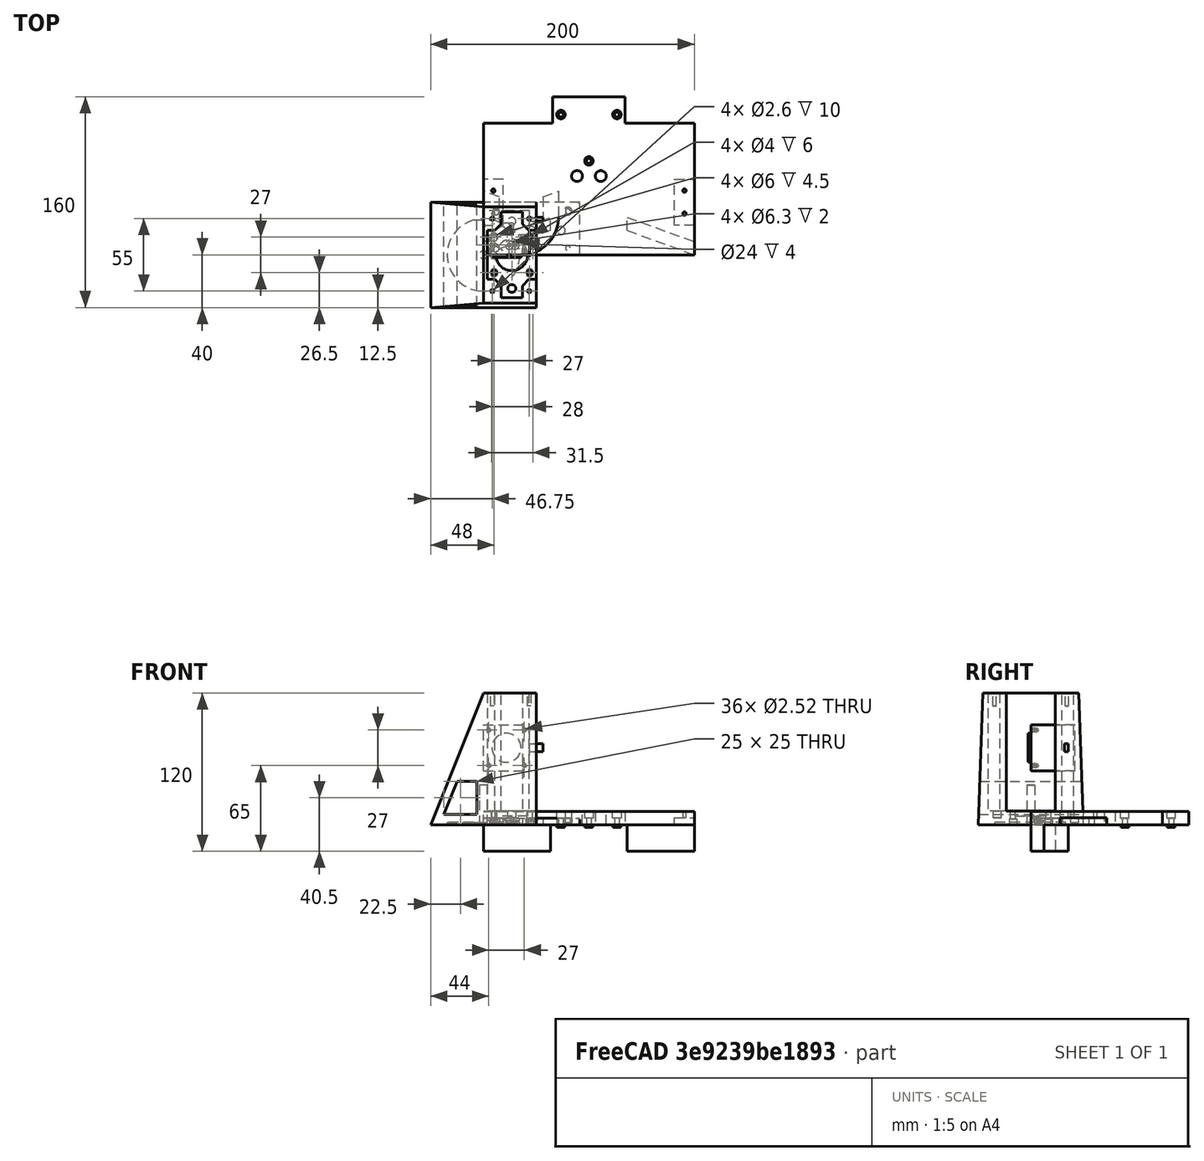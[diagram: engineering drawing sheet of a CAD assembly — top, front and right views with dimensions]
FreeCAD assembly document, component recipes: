
FREECAD ASSEMBLY — COMPONENT RECIPES ("charging-station")

This assembly document has 9 components, labeled P0..P8 below (a component is one placed body or linked part). 9 of them carry a construction recipe — the FreeCAD feature program that regenerates the part from scratch, quoted from this document or its linked companion documents; the rest are supplied as boundary geometry only. No exploded tour is included for this assembly.
COMPONENT P0 — recipe-attached ("Beam", modeled in this document).
Construction recipe (the document's own serialized feature program — sketch geometry with constraints, then the solid features built on it; lengths are millimeters unless a unit is written):

FEATURE [Sketcher::SketchObject] Sketch
  ArcFitTolerance = 0
  AttachmentSupport = -> [XY_Plane]
  FullyConstrained = true
  MakeInternals = false
  MapMode = 5
  sketch-geometry (4):
    g0: LineSegment StartX=0 StartY=0 StartZ=0 EndX=160 EndY=0 EndZ=0
    g1: LineSegment StartX=160 StartY=0 StartZ=0 EndX=160 EndY=100 EndZ=0
    g2: LineSegment StartX=160 StartY=100 StartZ=0 EndX=0 EndY=100 EndZ=0
    g3: LineSegment StartX=0 StartY=100 StartZ=0 EndX=0 EndY=0 EndZ=0
  constraints (11):
    c: Coincident(g0,g1)
    c: Coincident(g1,g2)
    c: Coincident(g2,g3)
    c: Coincident(g3,g0)
    c: Horizontal(g0)
    c: Horizontal(g2)
    c: Vertical(g1)
    c: Vertical(g3)
    c: Coincident(g0,g-1)
    c: DistanceY(g1,g1) = 100
    c: DistanceX(g0,g0) = 160
FEATURE [PartDesign::Pad] Pad
  Direction = (0,0,1)
  Length = 10
  Length2 = 10
  Profile = -> Sketch
  ReferenceAxis = -> Sketch [N_Axis]
  Suppressed = false
  Type = 0
FEATURE [Sketcher::SketchObject] Sketch001
  ArcFitTolerance = 0
  AttachmentSupport = -> [Pad]
  ExternalGeometry = -> [Pad]
  FullyConstrained = true
  MakeInternals = false
  MapMode = 5
  Placement = pos=(0,0,0) rot=(1,0,0;3.14159rad)
  sketch-geometry (15):
    g0: LineSegment [constr] StartX=63.5 StartY=-33.1121 StartZ=0 EndX=96.5 EndY=-33.1121 EndZ=0
    g1: LineSegment StartX=0 StartY=-10 StartZ=0 EndX=0 EndY=0 EndZ=0
    g2: LineSegment [constr] StartX=63.5 StartY=-23.1121 StartZ=0 EndX=63.5 EndY=-33.1121 EndZ=0
    g3: LineSegment [constr] StartX=96.5 StartY=-33.1121 StartZ=0 EndX=96.5 EndY=-23.1121 EndZ=0
    g4: LineSegment StartX=160 StartY=0 StartZ=0 EndX=160 EndY=-10 EndZ=0
    g5: LineSegment StartX=51 StartY=-18.5625 StartZ=0 EndX=51 EndY=-28.5625 EndZ=0
    g6: LineSegment StartX=0 StartY=-10 StartZ=0 EndX=51 EndY=-28.5625 EndZ=0
    g7: LineSegment [constr] StartX=51 StartY=-28.5625 StartZ=0 EndX=63.5 EndY=-33.1121 EndZ=0
    g8: LineSegment [constr] StartX=63.5 StartY=-23.1121 StartZ=0 EndX=51 EndY=-18.5625 EndZ=0
    g9: LineSegment StartX=51 StartY=-18.5625 StartZ=0 EndX=0 EndY=0 EndZ=0
    g10: LineSegment StartX=109 StartY=-18.5625 StartZ=0 EndX=109 EndY=-28.5625 EndZ=0
    g11: LineSegment [constr] StartX=96.5 StartY=-23.1121 StartZ=0 EndX=109 EndY=-18.5625 EndZ=0
    g12: LineSegment StartX=109 StartY=-18.5625 StartZ=0 EndX=160 EndY=0 EndZ=0
    g13: LineSegment [constr] StartX=96.5 StartY=-33.1121 StartZ=0 EndX=109 EndY=-28.5625 EndZ=0
    g14: LineSegment StartX=109 StartY=-28.5625 StartZ=0 EndX=160 EndY=-10 EndZ=0
  constraints (40):
    c: DistanceX(g0,g0) = 33
    c: Horizontal(g0)
    c: Vertical(g3)
    c: Vertical(g4)
    c: Vertical(g2)
    c: Equal(g2,g3)
    c: DistanceY(g4,g4) = 10
    c: Coincident(g1,g-1)
    c: Vertical(g1)
    c: Vertical(g5)
    c: DistanceX(g5,g0) = 12.5
    c: Coincident(g1,g6)
    c: Coincident(g6,g5)
    c: Coincident(g6,g7)
    c: Coincident(g7,g2)
    c: Coincident(g2,g8)
    c: Coincident(g8,g5)
    c: Coincident(g8,g9)
    c: Coincident(g9,g1)
    c: Vertical(g10)
    c: Coincident(g3,g11)
    c: Coincident(g11,g10)
    c: Coincident(g11,g12)
    c: Coincident(g3,g13)
    c: Coincident(g13,g10)
    c: Coincident(g13,g14)
    c: Coincident(g14,g4)
    c: Equal(g13,g7)
    c: Coincident(g2,g0)
    c: Coincident(g3,g0)
    c: Parallel(g6,g9)
    c: Parallel(g14,g12)
    c: Parallel(g7,g8)
    c: Parallel(g13,g11)
    c: Parallel(g13,g14)
    c: Parallel(g7,g6)
    c: Angle(g-1,g12) = 0.349066
    c: Equal(g14,g6)
    c: Coincident(g12,g-3)
    c: Coincident(g4,g12)
FEATURE [PartDesign::Pad] Pad008
  BaseFeature = -> Pad
  Direction = (0,0,-1)
  Length = 20
  Length2 = 10
  Profile = -> Sketch001
  ReferenceAxis = -> Sketch001 [N_Axis]
  Refine = true
  Suppressed = false
  Type = 0
FEATURE [Sketcher::SketchObject] Sketch029
  ArcFitTolerance = 0
  AttachmentSupport = -> [Pad008]
  ExternalGeometry = -> [Pad008]
  FullyConstrained = true
  MakeInternals = false
  MapMode = 5
  Placement = pos=(0,0,0) rot=(1,0,0;3.14159rad)
  sketch-geometry (16):
    g0: GeomPoint [constr] X=80 Y=-52.2941 Z=0
    g1: LineSegment [constr] StartX=80 StartY=-52.2941 StartZ=0 EndX=80 EndY=-59.7941 EndZ=0
    g2: LineSegment [constr] StartX=71 StartY=-59.7941 StartZ=0 EndX=89 EndY=-59.7941 EndZ=0
    g3: Circle CenterX=71 CenterY=-59.7941 CenterZ=0 NormalX=0 NormalY=0 NormalZ=1 AngleXU=0 Radius=4.15
    g4: Circle CenterX=89 CenterY=-59.7941 CenterZ=0 NormalX=0 NormalY=0 NormalZ=1 AngleXU=0 Radius=4.15
    g5: LineSegment [constr] StartX=51 StartY=-18.5625 StartZ=0 EndX=80 EndY=-29.1176 EndZ=0
    g6: LineSegment [constr] StartX=80 StartY=-29.1176 StartZ=0 EndX=109 EndY=-18.5625 EndZ=0
    g7: LineSegment [constr] StartX=51 StartY=-28.5625 StartZ=0 EndX=80 EndY=-39.1176 EndZ=0
    g8: LineSegment [constr] StartX=80 StartY=-39.1176 StartZ=0 EndX=109 EndY=-28.5625 EndZ=0
    g9: LineSegment [constr] StartX=64 StartY=-23.2941 StartZ=0 EndX=64 EndY=-43.2941 EndZ=0
    g10: LineSegment [constr] StartX=64 StartY=-43.2941 StartZ=0 EndX=74 EndY=-43.2941 EndZ=0
    g11: LineSegment [constr] StartX=74 StartY=-43.2941 StartZ=0 EndX=74 EndY=-52.2941 EndZ=0
    g12: LineSegment [constr] StartX=74 StartY=-52.2941 StartZ=0 EndX=86 EndY=-52.2941 EndZ=0
    g13: LineSegment [constr] StartX=86 StartY=-52.2941 StartZ=0 EndX=86 EndY=-43.2941 EndZ=0
    g14: LineSegment [constr] StartX=86 StartY=-43.2941 StartZ=0 EndX=96 EndY=-43.2941 EndZ=0
    g15: LineSegment [constr] StartX=96 StartY=-43.2941 StartZ=0 EndX=96 EndY=-23.2941 EndZ=0
  constraints (43):
    c: Coincident(g1,g0)
    c: Vertical(g1)
    c: Horizontal(g2)
    c: Symmetric(g2,g2,g1)
    c: Coincident(g3,g2)
    c: Coincident(g4,g2)
    c: Diameter(g4) = 8.3
    c: Equal(g4,g3)
    c: DistanceX(g2,g2) = 18
    c: Coincident(g5,g6)
    c: Angle(g5,g-1) = 0.349066
    c: Equal(g6,g5)
    c: Coincident(g7,g8)
    c: Parallel(g8,g6)
    c: Parallel(g7,g5)
    c: Coincident(g7,g-4)
    c: Vertical(g9)
    c: Coincident(g9,g10)
    c: Horizontal(g10)
    c: Coincident(g10,g11)
    c: Vertical(g11)
    c: Coincident(g11,g12)
    c: Horizontal(g12)
    c: Coincident(g12,g13)
    c: Coincident(g13,g14)
    c: Coincident(g14,g15)
    c: Vertical(g15)
    c: Horizontal(g14)
    c: Vertical(g13)
    c: Symmetric(g11,g12,g0)
    c: DistanceY(g15,g15) = 20
    c: Equal(g11,g13)
    c: Equal(g9,g15)
    c: Coincident(g5,g-3)
    c: DistanceY(g12,g14) = 9
    c: Equal(g10,g14)
    c: DistanceX(g12,g12) = 12
    c: DistanceY(g2,g12) = 7.5
    c: PointOnObject(g9,g5)
    c: PointOnObject(g15,g6)
    c: DistanceX(g9,g15) = 32
    c: Coincident(g8,g-5)
    c: Coincident(g6,g-5)
FEATURE [PartDesign::Pocket] Pocket017
  BaseFeature = -> Pad008
  Direction = (0,0,1)
  Length = 5
  Length2 = 5
  Profile = -> Sketch029
  ReferenceAxis = -> Sketch029 [N_Axis]
  Refine = true
  Suppressed = false
  Type = 2
FEATURE [Sketcher::SketchObject] Sketch031
  ArcFitTolerance = 0
  AttachmentSupport = -> [Pocket017]
  ExternalGeometry = -> [Pocket017]
  FullyConstrained = true
  MakeInternals = false
  MapMode = 5
  Placement = pos=(0,100,0) rot=(0,0.707107,0.707107;3.14159rad)
  sketch-geometry (6):
    g0: LineSegment StartX=-107.5 StartY=0 StartZ=0 EndX=-52.5 EndY=0 EndZ=0
    g1: LineSegment StartX=-52.5 StartY=0 StartZ=0 EndX=-52.5 EndY=10 EndZ=0
    g2: LineSegment StartX=-52.5 StartY=10 StartZ=0 EndX=-107.5 EndY=10 EndZ=0
    g3: LineSegment StartX=-107.5 StartY=10 StartZ=0 EndX=-107.5 EndY=0 EndZ=0
    g4: GeomPoint X=-80 Y=10 Z=0
    g5: GeomPoint X=-80 Y=10 Z=0
  constraints (13):
    c: Coincident(g0,g1)
    c: Coincident(g1,g2)
    c: Coincident(g2,g3)
    c: Coincident(g3,g0)
    c: Horizontal(g0)
    c: Horizontal(g2)
    c: Vertical(g1)
    c: Vertical(g3)
    c: PointOnObject(g0,g-1)
    c: Symmetric(g2,g2,g4)
    c: Symmetric(g-3,g-3,g5)
    c: Coincident(g4,g5)
    c: DistanceX(g2,g2) = 55
FEATURE [PartDesign::Pad] Pad010
  BaseFeature = -> Pocket017
  Direction = (0,1,-2e-16)
  Length = 20
  Length2 = 10
  Profile = -> Sketch031
  ReferenceAxis = -> Sketch031 [N_Axis]
  Refine = true
  Suppressed = false
  Type = 0
FEATURE [Sketcher::SketchObject] Sketch032
  ArcFitTolerance = 0
  AttachmentSupport = -> [Pad010]
  ExternalGeometry = -> [Pad010]
  FullyConstrained = true
  MakeInternals = false
  MapMode = 5
  Placement = pos=(0,0,-4e-16) rot=(1,0,0;3.14159rad)
  sketch-geometry (11):
    g0: Circle [constr] CenterX=80 CenterY=-95.2941 CenterZ=0 NormalX=0 NormalY=0 NormalZ=1 AngleXU=0 Radius=27.5
    g1: GeomPoint [constr] X=80 Y=-59.7941 Z=0
    g2: LineSegment [constr] StartX=80 StartY=-59.7941 StartZ=0 EndX=80 EndY=-95.2941 EndZ=0
    g3: LineSegment [constr] StartX=71 StartY=-67.7941 StartZ=0 EndX=89 EndY=-67.7941 EndZ=0
    g4: Circle CenterX=80 CenterY=-71.2941 CenterZ=0 NormalX=0 NormalY=0 NormalZ=1 AngleXU=0 Radius=3
    g5: Circle CenterX=101.25 CenterY=-106.449 CenterZ=0 NormalX=0 NormalY=0 NormalZ=1 AngleXU=0 Radius=3
    g6: Circle CenterX=58.75 CenterY=-106.449 CenterZ=0 NormalX=0 NormalY=0 NormalZ=1 AngleXU=0 Radius=3
    g7: LineSegment [constr] StartX=58.75 StartY=-106.449 StartZ=0 EndX=101.25 EndY=-106.449 EndZ=0
    g8: LineSegment [constr] StartX=80 StartY=-106.449 StartZ=0 EndX=80 EndY=-95.2941 EndZ=0
    g9: Circle [constr] CenterX=101.25 CenterY=-106.449 CenterZ=0 NormalX=0 NormalY=0 NormalZ=1 AngleXU=0 Radius=1.5
    g10: Circle [constr] CenterX=80 CenterY=-71.2941 CenterZ=0 NormalX=0 NormalY=0 NormalZ=1 AngleXU=0 Radius=1.5
  constraints (27):
    c: Diameter(g0) = 55
    c: Symmetric(g-4,g-3,g1)
    c: Coincident(g2,g1)
    c: Vertical(g2)
    c: Coincident(g0,g2)
    c: Horizontal(g3)
    c: Tangent(g3,g0)
    c: Distance(g-4,g3) = 8
    c: PointOnObject(g4,g2)
    c: Diameter(g4) = 6
    c: Equal(g6,g5)
    c: Equal(g5,g4)
    c: Horizontal(g6,g5)
    c: DistanceX(g6,g5) = 42.5
    c: Coincident(g7,g6)
    c: Coincident(g7,g5)
    c: Symmetric(g7,g7,g8)
    c: Coincident(g8,g0)
    c: Vertical(g8)
    c: Vertical(g3,g-3)
    c: Vertical(g3,g-4)
    c: Coincident(g9,g5)
    c: Diameter(g9) = 3
    c: Distance(g0,g9) = 2
    c: Coincident(g10,g4)
    c: Diameter(g10) = 3
    c: Distance(g10,g0) = 2
FEATURE [PartDesign::Pad] Pad011
  BaseFeature = -> Pad010
  Direction = (0,0,-1)
  Length = 2
  Length2 = 10
  Profile = -> Sketch032
  ReferenceAxis = -> Sketch032 [N_Axis]
  Refine = true
  Suppressed = false
  Type = 0
FEATURE [Sketcher::SketchObject] Sketch033
  ArcFitTolerance = 0
  AttachmentSupport = -> [Pad011]
  ExternalGeometry = -> [Pad011]
  FullyConstrained = true
  MakeInternals = false
  MapMode = 5
  Placement = pos=(0,0,-2) rot=(1,0,0;3.14159rad)
  sketch-geometry (3):
    g0: Circle CenterX=58.75 CenterY=-106.449 CenterZ=0 NormalX=0 NormalY=0 NormalZ=1 AngleXU=0 Radius=1.85
    g1: Circle CenterX=101.25 CenterY=-106.449 CenterZ=0 NormalX=0 NormalY=0 NormalZ=1 AngleXU=0 Radius=1.85
    g2: Circle CenterX=80 CenterY=-71.2941 CenterZ=0 NormalX=0 NormalY=0 NormalZ=1 AngleXU=0 Radius=1.85
  constraints (6):
    c: Coincident(g0,g-4)
    c: Coincident(g1,g-5)
    c: Coincident(g2,g-3)
    c: Equal(g2,g0)
    c: Equal(g0,g1)
    c: Diameter(g2) = 3.7
FEATURE [PartDesign::Pocket] Pocket018
  BaseFeature = -> Pad011
  Direction = (0,0,1)
  Length = 5
  Length2 = 5
  Profile = -> Sketch033
  ReferenceAxis = -> Sketch033 [N_Axis]
  Refine = true
  Suppressed = false
  Type = 1
FEATURE [Sketcher::SketchObject] Sketch034
  ArcFitTolerance = 0
  AttachmentSupport = -> [Pocket018]
  ExternalGeometry = -> [Pocket018]
  FullyConstrained = true
  MakeInternals = false
  MapMode = 5
  Placement = pos=(0,0,10) rot=(0,0,1;0rad)
  sketch-geometry (3):
    g0: Circle CenterX=58.75 CenterY=106.449 CenterZ=0 NormalX=0 NormalY=0 NormalZ=1 AngleXU=0 Radius=3.25
    g1: Circle CenterX=101.25 CenterY=106.449 CenterZ=0 NormalX=0 NormalY=0 NormalZ=1 AngleXU=0 Radius=3.25
    g2: Circle CenterX=80 CenterY=71.2941 CenterZ=0 NormalX=0 NormalY=0 NormalZ=1 AngleXU=0 Radius=3.25
  constraints (6):
    c: Coincident(g0,g-3)
    c: Equal(g2,g0)
    c: Equal(g0,g1)
    c: Diameter(g0) = 6.5
    c: Coincident(g1,g-5)
    c: Coincident(g2,g-4)
FEATURE [PartDesign::Pocket] Pocket019
  BaseFeature = -> Pocket018
  Direction = (0,0,-1)
  Length = 5
  Length2 = 5
  Profile = -> Sketch034
  ReferenceAxis = -> Sketch034 [N_Axis]
  Refine = true
  Suppressed = false
  Type = 0
FEATURE [Sketcher::SketchObject] Sketch035
  ArcFitTolerance = 0
  AttachmentSupport = -> [Pocket019]
  ExternalGeometry = -> [Pocket019]
  FullyConstrained = true
  MakeInternals = false
  MapMode = 5
  Placement = pos=(0,0,-4e-16) rot=(1,0,0;3.14159rad)
  sketch-geometry (12):
    g0: LineSegment StartX=145 StartY=-22.5 StartZ=0 EndX=145 EndY=-57.5 EndZ=0
    g1: LineSegment StartX=145 StartY=-57.5 StartZ=0 EndX=160 EndY=-57.5 EndZ=0
    g2: LineSegment StartX=160 StartY=-57.5 StartZ=0 EndX=160 EndY=-22.5 EndZ=0
    g3: LineSegment StartX=160 StartY=-22.5 StartZ=0 EndX=145 EndY=-22.5 EndZ=0
    g4: GeomPoint X=80 Y=0 Z=0
    g5: LineSegment [constr] StartX=80 StartY=0 StartZ=0 EndX=80 EndY=-100 EndZ=0
    g6: LineSegment StartX=0 StartY=-22.5 StartZ=0 EndX=15 EndY=-22.5 EndZ=0
    g7: LineSegment StartX=15 StartY=-22.5 StartZ=0 EndX=15 EndY=-57.5 EndZ=0
    g8: LineSegment StartX=15 StartY=-57.5 StartZ=0 EndX=0 EndY=-57.5 EndZ=0
    g9: LineSegment StartX=0 StartY=-57.5 StartZ=0 EndX=0 EndY=-22.5 EndZ=0
    g10: LineSegment [constr] StartX=0 StartY=0 StartZ=0 EndX=0 EndY=-22.5 EndZ=0
    g11: LineSegment [constr] StartX=160 StartY=-22.5 StartZ=0 EndX=160 EndY=0 EndZ=0
  constraints (31):
    c: Coincident(g0,g1)
    c: Coincident(g1,g2)
    c: Coincident(g2,g3)
    c: Coincident(g3,g0)
    c: Vertical(g0)
    c: Vertical(g2)
    c: Horizontal(g1)
    c: Horizontal(g3)
    c: DistanceY(g0,g0) = 35
    c: DistanceX(g3,g3) = 15
    c: PointOnObject(g2,g-3)
    c: DistanceY(g2,g-4) = 22.5
    c: Symmetric(g-4,g-4,g4)
    c: Coincident(g5,g4)
    c: Coincident(g7,g8)
    c: Coincident(g8,g9)
    c: Coincident(g9,g6)
    c: Coincident(g6,g7)
    c: Coincident(g-1,g10)
    c: Coincident(g10,g6)
    c: Vertical(g10)
    c: Coincident(g2,g11)
    c: Coincident(g11,g-4)
    c: Equal(g11,g10)
    c: Equal(g1,g8)
    c: Equal(g7,g0)
    c: Vertical(g7)
    c: Horizontal(g8)
    c: Horizontal(g6)
    c: Vertical(g9)
    c: Symmetric(g-6,g-5,g5)
FEATURE [PartDesign::Pocket] Pocket020
  BaseFeature = -> Pocket019
  Direction = (0,0,1)
  Length = 5.3
  Length2 = 5
  Profile = -> Sketch035
  ReferenceAxis = -> Sketch035 [N_Axis]
  Refine = true
  Suppressed = false
  Type = 0
FEATURE [Sketcher::SketchObject] Sketch036
  ArcFitTolerance = 0
  AttachmentSupport = -> [Pocket020]
  ExternalGeometry = -> [Pocket020]
  FullyConstrained = true
  MakeInternals = false
  MapMode = 5
  Placement = pos=(0,0,5.3) rot=(1,0,0;3.14159rad)
  sketch-geometry (12):
    g0: GeomPoint [constr] X=152.5 Y=-22.5 Z=0
    g1: GeomPoint [constr] X=152.5 Y=-57.5 Z=0
    g2: GeomPoint [constr] X=160 Y=-40 Z=0
    g3: GeomPoint [constr] X=145 Y=-40 Z=0
    g4: LineSegment [constr] StartX=145 StartY=-40 StartZ=0 EndX=160 EndY=-40 EndZ=0
    g5: GeomPoint [constr] X=152.5 Y=-40 Z=0
    g6: Circle CenterX=152.5 CenterY=-31.25 CenterZ=0 NormalX=0 NormalY=0 NormalZ=1 AngleXU=0 Radius=1.3
    g7: Circle CenterX=152.5 CenterY=-48.75 CenterZ=0 NormalX=0 NormalY=0 NormalZ=1 AngleXU=0 Radius=1.3
    g8: LineSegment [constr] StartX=7.5 StartY=-22.5 StartZ=0 EndX=7.5 EndY=-57.5 EndZ=0
    g9: GeomPoint [constr] X=7.5 Y=-40 Z=0
    g10: Circle CenterX=7.5 CenterY=-31.25 CenterZ=0 NormalX=0 NormalY=0 NormalZ=1 AngleXU=0 Radius=1.3
    g11: Circle CenterX=7.5 CenterY=-48.75 CenterZ=0 NormalX=0 NormalY=0 NormalZ=1 AngleXU=0 Radius=1.3
  constraints (18):
    c: Symmetric(g-3,g-3,g0)
    c: Symmetric(g-4,g-3,g2)
    c: Symmetric(g-4,g-4,g1)
    c: Symmetric(g-3,g-4,g3)
    c: Coincident(g4,g3)
    c: Coincident(g4,g2)
    c: Symmetric(g4,g4,g5)
    c: Symmetric(g5,g1,g7)
    c: Symmetric(g5,g0,g6)
    c: Equal(g7,g6)
    c: Diameter(g6) = 2.6
    c: Symmetric(g-5,g-5,g8)
    c: Symmetric(g-7,g-7,g8)
    c: Symmetric(g8,g8,g9)
    c: Symmetric(g9,g8,g11)
    c: Symmetric(g9,g8,g10)
    c: Equal(g10,g11)
    c: Equal(g6,g10)
FEATURE [PartDesign::Pocket] Pocket021
  BaseFeature = -> Pocket020
  Direction = (0,0,1)
  Length = 5
  Length2 = 5
  Profile = -> Sketch036
  ReferenceAxis = -> Sketch036 [N_Axis]
  Refine = true
  Suppressed = false
  Type = 1
FEATURE [PartDesign::Body] Body  label="beam"
  AllowCompound = false
  Group = -> [Sketch,Pad,Sketch001,Pad008,Sketch029,Pocket017,Sketch031,Pad010,Sketch032,Pad011,Sketch033,Pocket018,Sketch034,Pocket019,Sketch035,Pocket020,Sketch036,Pocket021]
  Origin = -> Origin
  Tip = -> Pocket021
COMPONENT P1 — recipe-attached ("BaseLeft", modeled in this document).
Construction recipe (the document's own serialized feature program — sketch geometry with constraints, then the solid features built on it; lengths are millimeters unless a unit is written):

FEATURE [Sketcher::SketchObject] Sketch007
  ArcFitTolerance = 0
  AttachmentSupport = -> [XY_Plane004]
  FullyConstrained = true
  MakeInternals = false
  MapMode = 5
  sketch-geometry (8):
    g0: LineSegment StartX=-40 StartY=40 StartZ=0 EndX=-40 EndY=-40 EndZ=0
    g1: LineSegment StartX=-40 StartY=-40 StartZ=0 EndX=40 EndY=-40 EndZ=0
    g2: LineSegment StartX=40 StartY=-40 StartZ=0 EndX=40 EndY=40 EndZ=0
    g3: LineSegment StartX=40 StartY=40 StartZ=0 EndX=-40 EndY=40 EndZ=0
    g4: LineSegment [constr] StartX=40 StartY=-40 StartZ=0 EndX=0 EndY=0 EndZ=0
    g5: LineSegment [constr] StartX=0 StartY=0 StartZ=0 EndX=-40 EndY=40 EndZ=0
    g6: LineSegment [constr] StartX=-40 StartY=-40 StartZ=0 EndX=0 EndY=0 EndZ=0
    g7: LineSegment [constr] StartX=0 StartY=0 StartZ=0 EndX=40 EndY=40 EndZ=0
  constraints (20):
    c: Coincident(g0,g1)
    c: Coincident(g1,g2)
    c: Coincident(g2,g3)
    c: Coincident(g3,g0)
    c: Vertical(g0)
    c: Vertical(g2)
    c: Horizontal(g1)
    c: Horizontal(g3)
    c: DistanceY(g2,g2) = 80
    c: DistanceX(g1,g1) = 80
    c: Coincident(g1,g4)
    c: Coincident(g4,g-1)
    c: Coincident(g4,g5)
    c: Coincident(g5,g0)
    c: Equal(g5,g4)
    c: Coincident(g0,g6)
    c: Coincident(g6,g4)
    c: Coincident(g6,g7)
    c: Coincident(g7,g2)
    c: Equal(g7,g6)
FEATURE [PartDesign::Pad] Pad005
  Direction = (0,0,1)
  Length = 100
  Length2 = 10
  Profile = -> Sketch007
  ReferenceAxis = -> Sketch007 [N_Axis]
  Refine = true
  Suppressed = false
  Type = 0
FEATURE [Sketcher::SketchObject] Sketch008
  ArcFitTolerance = 0
  AttachmentSupport = -> [Pad005]
  ExternalGeometry = -> [Pad005]
  FullyConstrained = true
  MakeInternals = false
  MapMode = 5
  Placement = pos=(0,-40,0) rot=(1,0,0;1.5708rad)
  sketch-geometry (10):
    g0: LineSegment StartX=-40 StartY=0 StartZ=0 EndX=0 EndY=100 EndZ=0
    g1: LineSegment [constr] StartX=0 StartY=100 StartZ=0 EndX=40 EndY=100 EndZ=0
    g2: LineSegment [constr] StartX=40 StartY=100 StartZ=0 EndX=40 EndY=0 EndZ=0
    g3: LineSegment [constr] StartX=40 StartY=0 StartZ=0 EndX=-40 EndY=0 EndZ=0
    g4: LineSegment StartX=0 StartY=100 StartZ=0 EndX=-40 EndY=100 EndZ=0
    g5: LineSegment StartX=-40 StartY=100 StartZ=0 EndX=-40 EndY=0 EndZ=0
    g6: LineSegment StartX=-30 StartY=8 StartZ=0 EndX=-5 EndY=8 EndZ=0
    g7: LineSegment StartX=-5 StartY=8 StartZ=0 EndX=-5 EndY=33 EndZ=0
    g8: LineSegment StartX=-20 StartY=33 StartZ=0 EndX=-30 EndY=8 EndZ=0
    g9: LineSegment StartX=-5 StartY=33 StartZ=0 EndX=-20 EndY=33 EndZ=0
  constraints (26):
    c: Coincident(g-4,g0)
    c: Coincident(g0,g1)
    c: Coincident(g1,g-5)
    c: Horizontal(g1)
    c: Coincident(g1,g2)
    c: Coincident(g2,g-5)
    c: Coincident(g2,g3)
    c: Coincident(g3,g0)
    c: DistanceX(g1,g1) = 40
    c: Coincident(g0,g4)
    c: Horizontal(g4)
    c: Coincident(g4,g5)
    c: Coincident(g5,g0)
    c: Vertical(g5)
    c: Horizontal(g6)
    c: Coincident(g6,g7)
    c: Vertical(g7)
    c: Coincident(g8,g6)
    c: DistanceX(g6,g-1) = 5
    c: DistanceY(g-1,g6) = 8
    c: DistanceX(g0,g6) = 10
    c: Parallel(g8,g0)
    c: Horizontal(g9)
    c: DistanceY(g6,g9) = 25
    c: Coincident(g7,g9)
    c: Coincident(g8,g9)
FEATURE [PartDesign::Pocket] Pocket001
  BaseFeature = -> Pad005
  Direction = (0,1,-2e-16)
  Length = 5
  Length2 = 5
  Profile = -> Sketch008
  ReferenceAxis = -> Sketch008 [N_Axis]
  Refine = true
  Suppressed = false
  Type = 1
FEATURE [Sketcher::SketchObject] Sketch009
  ArcFitTolerance = 0
  AttachmentSupport = -> [Pocket001]
  ExternalGeometry = -> [Pocket001]
  FullyConstrained = true
  MakeInternals = false
  MapMode = 5
  Placement = pos=(40,0,0) rot=(0.57735,0.57735,0.57735;2.0944rad)
  sketch-geometry (6):
    g0: LineSegment StartX=-36.5 StartY=100 StartZ=0 EndX=-40 EndY=0 EndZ=0
    g1: LineSegment StartX=40 StartY=0 StartZ=0 EndX=36.5 EndY=100 EndZ=0
    g2: LineSegment StartX=-36.5 StartY=100 StartZ=0 EndX=-40 EndY=100 EndZ=0
    g3: LineSegment StartX=-40 StartY=100 StartZ=0 EndX=-40 EndY=0 EndZ=0
    g4: LineSegment StartX=36.5 StartY=100 StartZ=0 EndX=40 EndY=100 EndZ=0
    g5: LineSegment StartX=40 StartY=100 StartZ=0 EndX=40 EndY=0 EndZ=0
  constraints (13):
    c: DistanceX(g0,g1) = 73
    c: Symmetric(g0,g1,g-2)
    c: Coincident(g-3,g1)
    c: PointOnObject(g1,g-4)
    c: Coincident(g0,g-3)
    c: Coincident(g0,g2)
    c: Coincident(g2,g-4)
    c: Coincident(g2,g3)
    c: Coincident(g3,g0)
    c: Coincident(g1,g4)
    c: Coincident(g4,g-4)
    c: Coincident(g4,g5)
    c: Coincident(g5,g1)
FEATURE [PartDesign::Pocket] Pocket002
  BaseFeature = -> Pocket001
  Direction = (-1,0,0)
  Length = 5
  Length2 = 5
  Profile = -> Sketch009
  ReferenceAxis = -> Sketch009 [N_Axis]
  Refine = true
  Suppressed = false
  Type = 1
FEATURE [Sketcher::SketchObject] Sketch011
  ArcFitTolerance = 0
  AttachmentSupport = -> [Pocket002]
  ExternalGeometry = -> [Pocket002]
  FullyConstrained = true
  MakeInternals = false
  MapMode = 5
  Placement = pos=(40,0,0) rot=(0.57735,0.57735,0.57735;2.0944rad)
  sketch-geometry (5):
    g0: LineSegment StartX=-18.5 StartY=10.5 StartZ=0 EndX=18.5 EndY=10.5 EndZ=0
    g1: LineSegment StartX=18.5 StartY=10.5 StartZ=0 EndX=18.5 EndY=1671.43 EndZ=0
    g2: LineSegment StartX=18.5 StartY=1671.43 StartZ=0 EndX=-18.5 EndY=1671.43 EndZ=0
    g3: LineSegment StartX=-18.5 StartY=1671.43 StartZ=0 EndX=-18.5 EndY=10.5 EndZ=0
    g4: GeomPoint X=0 Y=1671.43 Z=0
  constraints (13):
    c: Coincident(g0,g1)
    c: Coincident(g1,g2)
    c: Coincident(g2,g3)
    c: Coincident(g3,g0)
    c: Horizontal(g0)
    c: Horizontal(g2)
    c: Vertical(g1)
    c: Vertical(g3)
    c: PointOnObject(g1,g-3)
    c: DistanceX(g2,g2) = 37
    c: Symmetric(g2,g2,g4)
    c: PointOnObject(g4,g-2)
    c: DistanceY(g-1,g0) = 10.5
FEATURE [PartDesign::Pocket] Pocket003
  BaseFeature = -> Pocket002
  Direction = (-1,0,0)
  Length = 37
  Length2 = 5
  Profile = -> Sketch011
  ReferenceAxis = -> Sketch011 [N_Axis]
  Refine = true
  Suppressed = false
  Type = 0
FEATURE [Sketcher::SketchObject] Sketch012
  ArcFitTolerance = 0
  AttachmentSupport = -> [Pocket003]
  ExternalGeometry = -> [Pocket003]
  FullyConstrained = true
  MakeInternals = false
  MapMode = 5
  Placement = pos=(0,0,10.5) rot=(0,0,1;0rad)
  sketch-geometry (4):
    g0: Circle CenterX=21.5 CenterY=0 CenterZ=0 NormalX=0 NormalY=0 NormalZ=1 AngleXU=0 Radius=12
    g1: LineSegment [constr] StartX=3 StartY=18.5 StartZ=0 EndX=40 EndY=-18.5 EndZ=0
    g2: LineSegment [constr] StartX=40 StartY=18.5 StartZ=0 EndX=3 EndY=-18.5 EndZ=0
    g3: GeomPoint [constr] X=21.5 Y=0 Z=0
  constraints (7):
    c: Diameter(g0) = 24
    c: Coincident(g1,g-3)
    c: Coincident(g1,g-5)
    c: Coincident(g2,g-6)
    c: Coincident(g2,g-4)
    c: Symmetric(g1,g1,g3)
    c: Coincident(g3,g0)
FEATURE [PartDesign::Pocket] Pocket004
  BaseFeature = -> Pocket003
  Direction = (0,0,-1)
  Length = 4
  Length2 = 5
  Profile = -> Sketch012
  ReferenceAxis = -> Sketch012 [N_Axis]
  Refine = true
  Suppressed = false
  Type = 0
FEATURE [Sketcher::SketchObject] Sketch013
  ArcFitTolerance = 0
  AttachmentSupport = -> [Pocket004]
  ExternalGeometry = -> [Pocket004]
  FullyConstrained = true
  MakeInternals = false
  MapMode = 5
  Placement = pos=(0,0,10.5) rot=(0,0,1;0rad)
  sketch-geometry (20):
    g0: LineSegment [constr] StartX=3 StartY=18.5 StartZ=0 EndX=3 EndY=13.5 EndZ=0
    g1: LineSegment [constr] StartX=3 StartY=13.5 StartZ=0 EndX=8 EndY=13.5 EndZ=0
    g2: LineSegment [constr] StartX=8 StartY=13.5 StartZ=0 EndX=8 EndY=18.5 EndZ=0
    g3: LineSegment [constr] StartX=8 StartY=18.5 StartZ=0 EndX=3 EndY=18.5 EndZ=0
    g4: LineSegment [constr] StartX=35 StartY=13.5 StartZ=0 EndX=40 EndY=13.5 EndZ=0
    g5: LineSegment [constr] StartX=40 StartY=13.5 StartZ=0 EndX=40 EndY=18.5 EndZ=0
    g6: LineSegment [constr] StartX=40 StartY=18.5 StartZ=0 EndX=35 EndY=18.5 EndZ=0
    g7: LineSegment [constr] StartX=35 StartY=18.5 StartZ=0 EndX=35 EndY=13.5 EndZ=0
    g8: LineSegment [constr] StartX=3 StartY=-18.5 StartZ=0 EndX=8 EndY=-18.5 EndZ=0
    g9: LineSegment [constr] StartX=8 StartY=-18.5 StartZ=0 EndX=8 EndY=-13.5 EndZ=0
    g10: LineSegment [constr] StartX=8 StartY=-13.5 StartZ=0 EndX=3 EndY=-13.5 EndZ=0
    g11: LineSegment [constr] StartX=3 StartY=-13.5 StartZ=0 EndX=3 EndY=-18.5 EndZ=0
    g12: LineSegment [constr] StartX=35 StartY=-13.5 StartZ=0 EndX=35 EndY=-18.5 EndZ=0
    g13: LineSegment [constr] StartX=35 StartY=-18.5 StartZ=0 EndX=40 EndY=-18.5 EndZ=0
    g14: LineSegment [constr] StartX=40 StartY=-18.5 StartZ=0 EndX=40 EndY=-13.5 EndZ=0
    g15: LineSegment [constr] StartX=40 StartY=-13.5 StartZ=0 EndX=35 EndY=-13.5 EndZ=0
    g16: Circle CenterX=8 CenterY=13.5 CenterZ=0 NormalX=0 NormalY=0 NormalZ=1 AngleXU=0 Radius=2
    g17: Circle CenterX=35 CenterY=13.5 CenterZ=0 NormalX=0 NormalY=0 NormalZ=1 AngleXU=0 Radius=2
    g18: Circle CenterX=35 CenterY=-13.5 CenterZ=0 NormalX=0 NormalY=0 NormalZ=1 AngleXU=0 Radius=2
    g19: Circle CenterX=8 CenterY=-13.5 CenterZ=0 NormalX=0 NormalY=0 NormalZ=1 AngleXU=0 Radius=2
  constraints (52):
    c: Coincident(g0,g1)
    c: Coincident(g1,g2)
    c: Coincident(g2,g3)
    c: Coincident(g3,g0)
    c: Vertical(g0)
    c: Vertical(g2)
    c: Horizontal(g1)
    c: Horizontal(g3)
    c: Coincident(g0,g-4)
    c: Equal(g2,g1)
    c: DistanceY(g2,g2) = 5
    c: Coincident(g4,g5)
    c: Coincident(g5,g6)
    c: Coincident(g6,g7)
    c: Coincident(g7,g4)
    c: Horizontal(g4)
    c: Horizontal(g6)
    c: Vertical(g5)
    c: Vertical(g7)
    c: Coincident(g8,g9)
    c: Coincident(g9,g10)
    c: Coincident(g10,g11)
    c: Coincident(g11,g8)
    c: Horizontal(g8)
    c: Horizontal(g10)
    c: Vertical(g9)
    c: Vertical(g11)
    c: Coincident(g12,g13)
    c: Coincident(g13,g14)
    c: Coincident(g14,g15)
    c: Coincident(g15,g12)
    c: Vertical(g12)
    c: Vertical(g14)
    c: Horizontal(g13)
    c: Horizontal(g15)
    c: Equal(g7,g2)
    c: Equal(g4,g2)
    c: Coincident(g5,g-6)
    c: Coincident(g8,g-5)
    c: Equal(g10,g1)
    c: Equal(g10,g9)
    c: Equal(g12,g2)
    c: Equal(g15,g1)
    c: Coincident(g13,g-6)
    c: Coincident(g16,g1)
    c: Diameter(g16) = 4
    c: Coincident(g17,g4)
    c: Coincident(g18,g12)
    c: Coincident(g19,g9)
    c: Equal(g16,g17)
    c: Equal(g17,g18)
    c: Equal(g18,g19)
FEATURE [PartDesign::Pocket] Pocket005
  BaseFeature = -> Pocket004
  Direction = (0,0,-1)
  Length = 5
  Length2 = 5
  Profile = -> Sketch013
  ReferenceAxis = -> Sketch013 [N_Axis]
  Refine = true
  Suppressed = false
  Type = 1
FEATURE [Sketcher::SketchObject] Sketch014
  ArcFitTolerance = 0
  AttachmentSupport = -> [Pocket005]
  ExternalGeometry = -> [Pocket005]
  FullyConstrained = true
  MakeInternals = false
  MapMode = 5
  Placement = pos=(0,0,0) rot=(1,0,0;3.14159rad)
  sketch-geometry (4):
    g0: Circle CenterX=8 CenterY=13.5 CenterZ=0 NormalX=0 NormalY=0 NormalZ=1 AngleXU=0 Radius=3
    g1: Circle CenterX=35 CenterY=13.5 CenterZ=0 NormalX=0 NormalY=0 NormalZ=1 AngleXU=0 Radius=3
    g2: Circle CenterX=35 CenterY=-13.5 CenterZ=0 NormalX=0 NormalY=0 NormalZ=1 AngleXU=0 Radius=3
    g3: Circle CenterX=8 CenterY=-13.5 CenterZ=0 NormalX=0 NormalY=0 NormalZ=1 AngleXU=0 Radius=3
  constraints (8):
    c: Coincident(g0,g-3)
    c: Coincident(g1,g-4)
    c: Coincident(g2,g-5)
    c: Coincident(g3,g-6)
    c: Diameter(g0) = 6
    c: Equal(g0,g1)
    c: Equal(g1,g2)
    c: Equal(g2,g3)
FEATURE [PartDesign::Pocket] Pocket006
  BaseFeature = -> Pocket005
  Direction = (0,0,1)
  Length = 4.5
  Length2 = 5
  Profile = -> Sketch014
  ReferenceAxis = -> Sketch014 [N_Axis]
  Refine = true
  Suppressed = false
  Type = 0
FEATURE [Sketcher::SketchObject] Sketch016
  ArcFitTolerance = 0
  AttachmentSupport = -> [Pocket006]
  ExternalGeometry = -> [Pocket006]
  FullyConstrained = true
  MakeInternals = false
  MapMode = 5
  Placement = pos=(0,18.5,0) rot=(1,0,0;1.5708rad)
  sketch-geometry (6):
    g0: LineSegment StartX=13.5 StartY=100 StartZ=0 EndX=13.5 EndY=10.5 EndZ=0
    g1: LineSegment StartX=13.5 StartY=10.5 StartZ=0 EndX=29.5 EndY=10.5 EndZ=0
    g2: LineSegment StartX=29.5 StartY=10.5 StartZ=0 EndX=29.5 EndY=100 EndZ=0
    g3: LineSegment [constr] StartX=3 StartY=100 StartZ=0 EndX=13.5 EndY=100 EndZ=0
    g4: LineSegment [constr] StartX=29.5 StartY=100 StartZ=0 EndX=40 EndY=100 EndZ=0
    g5: LineSegment StartX=13.5 StartY=100 StartZ=0 EndX=29.5 EndY=100 EndZ=0
  constraints (16):
    c: Coincident(g0,g1)
    c: Coincident(g1,g2)
    c: Vertical(g0)
    c: Vertical(g2)
    c: Horizontal(g1)
    c: Equal(g4,g3)
    c: DistanceX(g0,g2) = 16
    c: Coincident(g2,g4)
    c: Coincident(g3,g0)
    c: Horizontal(g3)
    c: Coincident(g0,g5)
    c: Coincident(g5,g2)
    c: Coincident(g3,g-3)
    c: Coincident(g4,g-3)
    c: PointOnObject(g2,g-3)
    c: PointOnObject(g1,g-4)
FEATURE [PartDesign::Pocket] Pocket008
  BaseFeature = -> Pocket006
  Direction = (0,1,-2e-16)
  Length = 14
  Length2 = 5
  Profile = -> Sketch016
  ReferenceAxis = -> Sketch016 [N_Axis]
  Refine = true
  Suppressed = false
  Type = 0
FEATURE [Sketcher::SketchObject] Sketch024
  ArcFitTolerance = 0
  AttachmentSupport = -> [Pocket008]
  ExternalGeometry = -> [Pocket008]
  FullyConstrained = true
  MakeInternals = false
  MapMode = 5
  Placement = pos=(0,-18.5,0) rot=(0,0.707107,0.707107;3.14159rad)
  sketch-geometry (6):
    g0: LineSegment StartX=-29.5 StartY=10.5 StartZ=0 EndX=-13.5 EndY=10.5 EndZ=0
    g1: LineSegment StartX=-13.5 StartY=10.5 StartZ=0 EndX=-13.5 EndY=100 EndZ=0
    g2: LineSegment StartX=-13.5 StartY=100 StartZ=0 EndX=-29.5 EndY=100 EndZ=0
    g3: LineSegment StartX=-29.5 StartY=100 StartZ=0 EndX=-29.5 EndY=10.5 EndZ=0
    g4: LineSegment [constr] StartX=-40 StartY=100 StartZ=0 EndX=-29.5 EndY=100 EndZ=0
    g5: LineSegment [constr] StartX=-13.5 StartY=100 StartZ=0 EndX=-3 EndY=100 EndZ=0
  constraints (16):
    c: Coincident(g2,g3)
    c: Coincident(g3,g0)
    c: Horizontal(g0)
    c: Horizontal(g2)
    c: Vertical(g1)
    c: Vertical(g3)
    c: PointOnObject(g1,g-3)
    c: DistanceX(g2,g2) = 16
    c: PointOnObject(g0,g-5)
    c: Coincident(g1,g2)
    c: Coincident(g1,g0)
    c: Coincident(g-3,g4)
    c: Coincident(g4,g2)
    c: Coincident(g1,g5)
    c: Coincident(g5,g-4)
    c: Equal(g5,g4)
FEATURE [PartDesign::Pocket] Pocket015
  BaseFeature = -> Pocket008
  Direction = (0,-1,2e-16)
  Length = 14
  Length2 = 5
  Profile = -> Sketch024
  ReferenceAxis = -> Sketch024 [N_Axis]
  Refine = true
  Suppressed = false
  Type = 0
FEATURE [Sketcher::SketchObject] Sketch018
  ArcFitTolerance = 0
  AttachmentSupport = -> [Pocket015]
  ExternalGeometry = -> [Pocket015]
  FullyConstrained = true
  MakeInternals = false
  MapMode = 5
  Placement = pos=(0,0,10.5) rot=(0,0,1;0rad)
  sketch-geometry (4):
    g0: LineSegment [constr] StartX=13.5 StartY=-18.5 StartZ=0 EndX=29.5 EndY=-32.5 EndZ=0
    g1: LineSegment [constr] StartX=13.5 StartY=18.5 StartZ=0 EndX=29.5 EndY=32.5 EndZ=0
    g2: Circle CenterX=21.5 CenterY=-25.5 CenterZ=0 NormalX=0 NormalY=0 NormalZ=1 AngleXU=0 Radius=3
    g3: Circle CenterX=21.5 CenterY=25.5 CenterZ=0 NormalX=0 NormalY=0 NormalZ=1 AngleXU=0 Radius=3
  constraints (8):
    c: Symmetric(g0,g0,g2)
    c: Diameter(g2) = 6
    c: Symmetric(g1,g1,g3)
    c: Equal(g3,g2)
    c: Coincident(g1,g-5)
    c: Coincident(g1,g-4)
    c: Coincident(g0,g-3)
    c: Coincident(g0,g-6)
FEATURE [PartDesign::Pocket] Pocket010
  BaseFeature = -> Pocket015
  Direction = (0,0,-1)
  Length = 5
  Length2 = 5
  Profile = -> Sketch018
  ReferenceAxis = -> Sketch018 [N_Axis]
  Refine = true
  Suppressed = false
  Type = 0
FEATURE [Sketcher::SketchObject] Sketch022
  ArcFitTolerance = 0
  AttachmentSupport = -> [Pocket010]
  ExternalGeometry = -> [Pocket010]
  FullyConstrained = true
  MakeInternals = false
  MapMode = 5
  Placement = pos=(0,0,100) rot=(0,0,1;0rad)
  sketch-geometry (8):
    g0: LineSegment [constr] StartX=13.5 StartY=18.5 StartZ=0 EndX=0 EndY=36.5 EndZ=0
    g1: LineSegment [constr] StartX=0 StartY=-36.5 StartZ=0 EndX=13.5 EndY=-18.5 EndZ=0
    g2: LineSegment [constr] StartX=29.5 StartY=-18.5 StartZ=0 EndX=40 EndY=-36.5 EndZ=0
    g3: LineSegment [constr] StartX=29.5 StartY=18.5 StartZ=0 EndX=40 EndY=36.5 EndZ=0
    g4: Circle CenterX=6.75 CenterY=27.5 CenterZ=0 NormalX=0 NormalY=0 NormalZ=1 AngleXU=0 Radius=1.3
    g5: Circle CenterX=34.75 CenterY=27.5 CenterZ=0 NormalX=0 NormalY=0 NormalZ=1 AngleXU=0 Radius=1.3
    g6: Circle CenterX=6.75 CenterY=-27.5 CenterZ=0 NormalX=0 NormalY=0 NormalZ=1 AngleXU=0 Radius=1.3
    g7: Circle CenterX=34.75 CenterY=-27.5 CenterZ=0 NormalX=0 NormalY=0 NormalZ=1 AngleXU=0 Radius=1.3
  constraints (16):
    c: Coincident(g1,g-8)
    c: Coincident(g1,g-9)
    c: Coincident(g2,g-9)
    c: Coincident(g2,g-10)
    c: Symmetric(g2,g2,g7)
    c: Symmetric(g1,g1,g6)
    c: Coincident(g0,g-12)
    c: Coincident(g0,g-13)
    c: Symmetric(g0,g0,g4)
    c: Symmetric(g3,g3,g5)
    c: Coincident(g3,g-11)
    c: Coincident(g3,g-13)
    c: Equal(g7,g6)
    c: Equal(g6,g4)
    c: Equal(g4,g5)
    c: Diameter(g4) = 2.6
FEATURE [PartDesign::Pocket] Pocket013
  BaseFeature = -> Pocket010
  Direction = (0,0,-1)
  Length = 10
  Length2 = 5
  Profile = -> Sketch022
  ReferenceAxis = -> Sketch022 [N_Axis]
  Refine = true
  Suppressed = false
  Type = 0
FEATURE [PartDesign::Chamfer] Chamfer
  Angle = 45
  Base = -> Pocket013 [Edge75,Edge82,Edge87,Edge56]
  BaseFeature = -> Pocket013
  ChamferType = 0
  FlipDirection = false
  Refine = true
  Size = 5
  Size2 = 1
  SupportTransform = false
  Suppressed = false
  UseAllEdges = false
FEATURE [PartDesign::Body] Body006  label="base"
  AllowCompound = false
  Group = -> [Sketch007,Pad005,Sketch008,Pocket001,Sketch009,Pocket002,Sketch011,Pocket003,Sketch012,Pocket004,Sketch013,Pocket005,Sketch014,Pocket006,Sketch016,Pocket008,Sketch024,Pocket015,Sketch018,Pocket010,Sketch022,Pocket013,Chamfer]
  Origin = -> Origin004
  Tip = -> Chamfer
COMPONENT P2 — same part as P1; its construction recipe is shown at P1.
COMPONENT P3 — recipe-attached ("BaseTopLeft", modeled in this document).
Construction recipe (the document's own serialized feature program — sketch geometry with constraints, then the solid features built on it; lengths are millimeters unless a unit is written):

FEATURE [Sketcher::SketchObject] Sketch019
  ArcFitTolerance = 0
  AttachmentSupport = -> [XY_Plane005]
  FullyConstrained = true
  MakeInternals = false
  MapMode = 5
  sketch-geometry (4):
    g0: LineSegment StartX=0 StartY=0 StartZ=0 EndX=73 EndY=0 EndZ=0
    g1: LineSegment StartX=73 StartY=0 StartZ=0 EndX=73 EndY=40 EndZ=0
    g2: LineSegment StartX=73 StartY=40 StartZ=0 EndX=0 EndY=40 EndZ=0
    g3: LineSegment StartX=0 StartY=40 StartZ=0 EndX=0 EndY=0 EndZ=0
  constraints (11):
    c: Coincident(g0,g1)
    c: Coincident(g1,g2)
    c: Coincident(g2,g3)
    c: Coincident(g3,g0)
    c: Horizontal(g0)
    c: Horizontal(g2)
    c: Vertical(g1)
    c: Vertical(g3)
    c: Coincident(g0,g-1)
    c: DistanceY(g1,g1) = 40
    c: DistanceX(g2,g2) = 73
FEATURE [PartDesign::Pad] Pad006
  Direction = (0,0,1)
  Length = 5
  Length2 = 10
  Profile = -> Sketch019
  ReferenceAxis = -> Sketch019 [N_Axis]
  Refine = true
  Suppressed = false
  Type = 0
FEATURE [Sketcher::SketchObject] Sketch020
  ArcFitTolerance = 0
  AttachmentSupport = -> [Pad006]
  ExternalGeometry = -> [Pad006]
  FullyConstrained = true
  MakeInternals = false
  MapMode = 5
  Placement = pos=(0,0,5) rot=(0,0,1;0rad)
  sketch-geometry (35):
    g0: LineSegment [constr] StartX=0 StartY=0 StartZ=0 EndX=18 EndY=0 EndZ=0
    g1: LineSegment [constr] StartX=18 StartY=0 StartZ=0 EndX=18 EndY=10.5 EndZ=0
    g2: LineSegment [constr] StartX=18 StartY=10.5 StartZ=0 EndX=0 EndY=10.5 EndZ=0
    g3: LineSegment [constr] StartX=0 StartY=10.5 StartZ=0 EndX=0 EndY=0 EndZ=0
    g4: LineSegment [constr] StartX=0 StartY=40 StartZ=0 EndX=0 EndY=26.5 EndZ=0
    g5: LineSegment [constr] StartX=0 StartY=26.5 StartZ=0 EndX=18 EndY=26.5 EndZ=0
    g6: LineSegment [constr] StartX=18 StartY=26.5 StartZ=0 EndX=18 EndY=37 EndZ=0
    g7: LineSegment [constr] StartX=18 StartY=40 StartZ=0 EndX=0 EndY=40 EndZ=0
    g8: LineSegment [constr] StartX=73 StartY=40 StartZ=0 EndX=55 EndY=40 EndZ=0
    g9: LineSegment [constr] StartX=55 StartY=37 StartZ=0 EndX=55 EndY=26.5 EndZ=0
    g10: LineSegment [constr] StartX=55 StartY=26.5 StartZ=0 EndX=73 EndY=26.5 EndZ=0
    g11: LineSegment [constr] StartX=73 StartY=26.5 StartZ=0 EndX=73 EndY=40 EndZ=0
    g12: LineSegment [constr] StartX=73 StartY=0 StartZ=0 EndX=73 EndY=10.5 EndZ=0
    g13: LineSegment [constr] StartX=73 StartY=10.5 StartZ=0 EndX=55 EndY=10.5 EndZ=0
    g14: LineSegment [constr] StartX=55 StartY=10.5 StartZ=0 EndX=55 EndY=0 EndZ=0
    g15: LineSegment [constr] StartX=55 StartY=0 StartZ=0 EndX=73 EndY=0 EndZ=0
    g16: Circle CenterX=14 CenterY=18.5 CenterZ=0 NormalX=0 NormalY=0 NormalZ=1 AngleXU=0 Radius=3
    g17: Circle CenterX=59 CenterY=18.5 CenterZ=0 NormalX=0 NormalY=0 NormalZ=1 AngleXU=0 Radius=3
    g18: Circle CenterX=36.5 CenterY=18.5 CenterZ=0 NormalX=0 NormalY=0 NormalZ=1 AngleXU=0 Radius=3
    g19: Circle CenterX=9 CenterY=33.25 CenterZ=0 NormalX=0 NormalY=0 NormalZ=1 AngleXU=0 Radius=1.75
    g20: Circle CenterX=64 CenterY=33.25 CenterZ=0 NormalX=0 NormalY=0 NormalZ=1 AngleXU=0 Radius=1.75
    g21: Circle CenterX=64 CenterY=5.25 CenterZ=0 NormalX=0 NormalY=0 NormalZ=1 AngleXU=0 Radius=1.75
    g22: Circle CenterX=9 CenterY=5.25 CenterZ=0 NormalX=0 NormalY=0 NormalZ=1 AngleXU=0 Radius=1.75
    g23: LineSegment [constr] StartX=0 StartY=26.5 StartZ=0 EndX=0 EndY=10.5 EndZ=0
    g24: LineSegment [constr] StartX=0 StartY=10.5 StartZ=0 EndX=10 EndY=10.5 EndZ=0
    g25: LineSegment [constr] StartX=10 StartY=10.5 StartZ=0 EndX=10 EndY=26.5 EndZ=0
    g26: LineSegment [constr] StartX=10 StartY=26.5 StartZ=0 EndX=0 EndY=26.5 EndZ=0
    g27: LineSegment [constr] StartX=73 StartY=10.5 StartZ=0 EndX=73 EndY=26.5 EndZ=0
    g28: LineSegment [constr] StartX=73 StartY=26.5 StartZ=0 EndX=63 EndY=26.5 EndZ=0
    g29: LineSegment [constr] StartX=63 StartY=26.5 StartZ=0 EndX=63 EndY=10.5 EndZ=0
    g30: LineSegment [constr] StartX=63 StartY=10.5 StartZ=0 EndX=73 EndY=10.5 EndZ=0
    g31: LineSegment [constr] StartX=18 StartY=40 StartZ=0 EndX=18 EndY=37 EndZ=0
    g32: LineSegment [constr] StartX=18 StartY=37 StartZ=0 EndX=55 EndY=37 EndZ=0
    g33: LineSegment [constr] StartX=55 StartY=37 StartZ=0 EndX=55 EndY=40 EndZ=0
    g34: LineSegment [constr] StartX=55 StartY=40 StartZ=0 EndX=18 EndY=40 EndZ=0
  constraints (92):
    c: Coincident(g0,g1)
    c: Coincident(g1,g2)
    c: Coincident(g2,g3)
    c: Coincident(g3,g0)
    c: Horizontal(g0)
    c: Horizontal(g2)
    c: Vertical(g1)
    c: Vertical(g3)
    c: Coincident(g0,g-1)
    c: Coincident(g4,g5)
    c: Coincident(g5,g6)
    c: Vertical(g4)
    c: Vertical(g6)
    c: Horizontal(g5)
    c: Horizontal(g7)
    c: Coincident(g9,g10)
    c: Coincident(g10,g11)
    c: Coincident(g11,g8)
    c: Horizontal(g8)
    c: Horizontal(g10)
    c: Vertical(g9)
    c: Vertical(g11)
    c: Coincident(g8,g-5)
    c: Coincident(g12,g13)
    c: Coincident(g13,g14)
    c: Coincident(g14,g15)
    c: Coincident(g15,g12)
    c: Vertical(g12)
    c: Vertical(g14)
    c: Horizontal(g13)
    c: Horizontal(g15)
    c: Coincident(g12,g-6)
    c: DistanceY(g2,g4) = 16
    c: DistanceX(g-1,g0) = 18
    c: Symmetric(g25,g1,g16)
    c: Symmetric(g9,g29,g17)
    c: Symmetric(g5,g13,g18)
    c: Diameter(g18) = 6
    c: Diameter(g16) = 6
    c: Equal(g16,g17)
    c: Symmetric(g13,g12,g21)
    c: Diameter(g19) = 3.5
    c: Coincident(g23,g24)
    c: Coincident(g24,g25)
    c: Coincident(g25,g26)
    c: Coincident(g26,g23)
    c: Vertical(g23)
    c: Vertical(g25)
    c: Horizontal(g24)
    c: Horizontal(g26)
    c: Coincident(g23,g4)
    c: PointOnObject(g24,g2)
    c: DistanceX(g24,g1) = 8
    c: Coincident(g27,g28)
    c: Coincident(g28,g29)
    c: Coincident(g29,g30)
    c: Coincident(g30,g27)
    c: Vertical(g27)
    c: Vertical(g29)
    c: Horizontal(g28)
    c: Horizontal(g30)
    c: Coincident(g27,g12)
    c: PointOnObject(g28,g10)
    c: DistanceX(g13,g29) = 8
    c: Coincident(g31,g32)
    c: Coincident(g32,g33)
    c: Coincident(g33,g34)
    c: Coincident(g34,g31)
    c: Vertical(g31)
    c: Vertical(g33)
    c: Horizontal(g32)
    c: Coincident(g31,g7)
    c: Coincident(g-4,g7)
    c: Coincident(g4,g7)
    c: Distance(g32,g8) = 3
    c: DistanceY(g5,g31) = 10.5
    c: DistanceY(g5,g7) = 13.5
    c: Symmetric(g5,g4,g19)
    c: Symmetric(g0,g1,g22)
    c: Symmetric(g9,g8,g20)
    c: Equal(g19,g22)
    c: Equal(g22,g21)
    c: Equal(g21,g20)
    c: Coincident(g9,g32)
    c: Equal(g6,g9)
    c: Equal(g14,g1)
    c: Equal(g1,g6)
    c: Coincident(g6,g31)
    c: Equal(g5,g10)
    c: Equal(g10,g13)
    c: Equal(g13,g2)
    c: Coincident(g8,g33)
FEATURE [PartDesign::Pocket] Pocket011
  BaseFeature = -> Pad006
  Direction = (0,0,-1)
  Length = 5
  Length2 = 5
  Profile = -> Sketch020
  ReferenceAxis = -> Sketch020 [N_Axis]
  Refine = true
  Suppressed = false
  Type = 2
FEATURE [Sketcher::SketchObject] Sketch021
  ArcFitTolerance = 0
  AttachmentSupport = -> [Pocket011]
  ExternalGeometry = -> [Pocket011]
  FullyConstrained = true
  MakeInternals = false
  MapMode = 5
  Placement = pos=(0,0,5) rot=(0,0,1;0rad)
  sketch-geometry (4):
    g0: Circle CenterX=36.5 CenterY=18.5 CenterZ=0 NormalX=0 NormalY=0 NormalZ=1 AngleXU=0 Radius=3
    g1: Circle CenterX=9 CenterY=5.25 CenterZ=0 NormalX=0 NormalY=0 NormalZ=1 AngleXU=0 Radius=3
    g2: Circle CenterX=64 CenterY=33.25 CenterZ=0 NormalX=0 NormalY=0 NormalZ=1 AngleXU=0 Radius=3
    g3: Circle CenterX=9 CenterY=33.25 CenterZ=0 NormalX=0 NormalY=0 NormalZ=1 AngleXU=0 Radius=3
  constraints (8):
    c: Coincident(g1,g-3)
    c: Coincident(g2,g-4)
    c: Diameter(g0) = 6
    c: Equal(g0,g2)
    c: Equal(g2,g3)
    c: Equal(g3,g1)
    c: Coincident(g3,g-5)
    c: Coincident(g0,g-6)
FEATURE [PartDesign::Pocket] Pocket012
  BaseFeature = -> Pocket011
  Direction = (0,0,-1)
  Length = 3.5
  Length2 = 5
  Profile = -> Sketch021
  ReferenceAxis = -> Sketch021 [N_Axis]
  Refine = true
  Suppressed = false
  Type = 0
FEATURE [PartDesign::Fillet] Fillet
  Base = -> Pocket012 [Edge10,Edge19,Edge7,Edge4]
  BaseFeature = -> Pocket012
  Radius = 1
  Refine = true
  SupportTransform = false
  Suppressed = false
  UseAllEdges = false
FEATURE [Sketcher::SketchObject] Sketch023
  ArcFitTolerance = 0
  AttachmentSupport = -> [Fillet]
  ExternalGeometry = -> [Fillet]
  FullyConstrained = true
  MakeInternals = false
  MapMode = 5
  Placement = pos=(0,0,5) rot=(0,0,1;0rad)
  sketch-geometry (5):
    g0: LineSegment [constr] StartX=36.5 StartY=1 StartZ=0 EndX=36.5 EndY=4 EndZ=0
    g1: LineSegment StartX=36.5 StartY=4 StartZ=0 EndX=38.5 EndY=7 EndZ=0
    g2: LineSegment StartX=38.5 StartY=7 StartZ=0 EndX=34.5 EndY=7 EndZ=0
    g3: LineSegment StartX=34.5 StartY=7 StartZ=0 EndX=36.5 EndY=4 EndZ=0
    g4: LineSegment [constr] StartX=36.5 StartY=7 StartZ=0 EndX=36.5 EndY=4 EndZ=0
  constraints (13):
    c: Coincident(g1,g2)
    c: Horizontal(g2)
    c: Coincident(g2,g3)
    c: Coincident(g3,g1)
    c: DistanceX(g2,g2) = 4
    c: Vertical(g0)
    c: Coincident(g1,g0)
    c: DistanceY(g0,g0) = 3
    c: Symmetric(g-3,g-3,g0)
    c: Symmetric(g2,g2,g4)
    c: Coincident(g4,g0)
    c: Vertical(g4)
    c: DistanceY(g0,g1) = 3
FEATURE [PartDesign::Pocket] Pocket014
  BaseFeature = -> Fillet
  Direction = (0,0,-1)
  Length = 1
  Length2 = 5
  Profile = -> Sketch023
  ReferenceAxis = -> Sketch023 [N_Axis]
  Refine = true
  Suppressed = false
  Type = 0
FEATURE [PartDesign::Body] Body007  label="base-top"
  AllowCompound = false
  Group = -> [Sketch019,Pad006,Sketch020,Pocket011,Sketch021,Pocket012,Fillet,Sketch023,Pocket014]
  Origin = -> Origin005
  Tip = -> Pocket014
COMPONENT P4 — same part as P3; its construction recipe is shown at P3.
COMPONENT P5 — recipe-attached ("Claw", modeled in this document).
Construction recipe (the document's own serialized feature program — sketch geometry with constraints, then the solid features built on it; lengths are millimeters unless a unit is written):

FEATURE [Sketcher::SketchObject] Sketch025
  ArcFitTolerance = 0
  AttachmentSupport = -> [XY_Plane006]
  FullyConstrained = true
  MakeInternals = false
  MapMode = 5
  sketch-geometry (8):
    g0: LineSegment [constr] StartX=0 StartY=0 StartZ=0 EndX=57 EndY=0 EndZ=0
    g1: LineSegment [constr] StartX=57 StartY=0 StartZ=0 EndX=57 EndY=57 EndZ=0
    g2: LineSegment [constr] StartX=57 StartY=57 StartZ=0 EndX=0 EndY=57 EndZ=0
    g3: LineSegment [constr] StartX=0 StartY=57 StartZ=0 EndX=0 EndY=0 EndZ=0
    g4: LineSegment StartX=0 StartY=28.5 StartZ=0 EndX=0 EndY=57 EndZ=0
    g5: LineSegment StartX=0 StartY=57 StartZ=0 EndX=57 EndY=57 EndZ=0
    g6: ArcOfCircle CenterX=28.5 CenterY=28.5 CenterZ=0 NormalX=0 NormalY=0 NormalZ=1 AngleXU=0 Radius=28.5 StartAngle=3.14159 EndAngle=6.28319
    g7: LineSegment StartX=57 StartY=57 StartZ=0 EndX=57 EndY=28.5 EndZ=0
  constraints (22):
    c: Coincident(g0,g1)
    c: Coincident(g1,g2)
    c: Coincident(g2,g3)
    c: Coincident(g3,g0)
    c: Horizontal(g0)
    c: Horizontal(g2)
    c: Vertical(g1)
    c: Coincident(g0,g-1)
    c: DistanceX(g2,g2) = 57
    c: Equal(g1,g2)
    c: Symmetric(g3,g3,g4)
    c: Coincident(g4,g2)
    c: Vertical(g4)
    c: Coincident(g4,g5)
    c: Horizontal(g5)
    c: Coincident(g6,g4)
    c: Tangent(g6,g0)
    c: Coincident(g5,g7)
    c: PointOnObject(g7,g1)
    c: Vertical(g7)
    c: Coincident(g6,g7)
    c: Equal(g7,g4)
FEATURE [PartDesign::Pad] Pad007
  Direction = (0,0,1)
  Length = 5
  Length2 = 10
  Profile = -> Sketch025
  ReferenceAxis = -> Sketch025 [N_Axis]
  Refine = true
  Suppressed = false
  Type = 0
FEATURE [Sketcher::SketchObject] Sketch026
  ArcFitTolerance = 0
  AttachmentSupport = -> [Pad007]
  ExternalGeometry = -> [Pad007]
  FullyConstrained = true
  MakeInternals = false
  MapMode = 5
  Placement = pos=(0,0,5) rot=(0,0,1;0rad)
  sketch-geometry (22):
    g0: ArcOfCircle [constr] CenterX=28.5 CenterY=28.5 CenterZ=0 NormalX=0 NormalY=0 NormalZ=1 AngleXU=0 Radius=27.5 StartAngle=1.8413 EndAngle=7.58348
    g1: LineSegment [constr] StartX=21.1515 StartY=55 StartZ=0 EndX=35.8485 EndY=55 EndZ=0
    g2: LineSegment [constr] StartX=28.5 StartY=55 StartZ=0 EndX=28.5 EndY=1 EndZ=0
    g3: GeomPoint [constr] X=28.5 Y=15 Z=0
    g4: GeomPoint [constr] X=28.5 Y=24 Z=0
    g5: LineSegment StartX=22.5 StartY=15 StartZ=0 EndX=34.5 EndY=15 EndZ=0
    g6: LineSegment StartX=12 StartY=24 StartZ=0 EndX=22.5 EndY=24 EndZ=0
    g7: LineSegment StartX=45 StartY=24 StartZ=0 EndX=45 EndY=44 EndZ=0
    g8: LineSegment StartX=45 StartY=57 StartZ=0 EndX=12 EndY=57 EndZ=0
    g9: LineSegment StartX=22.5 StartY=15 StartZ=0 EndX=22.5 EndY=24 EndZ=0
    g10: LineSegment StartX=34.5 StartY=15 StartZ=0 EndX=34.5 EndY=24 EndZ=0
    g11: LineSegment [constr] StartX=0 StartY=28.5 StartZ=0 EndX=56 EndY=28.5 EndZ=0
    g12: LineSegment StartX=34.5 StartY=24 StartZ=0 EndX=45 EndY=24 EndZ=0
    g13: LineSegment StartX=12 StartY=57 StartZ=0 EndX=-23.7172 EndY=57 EndZ=0
    g14: LineSegment StartX=45 StartY=57 StartZ=0 EndX=80.7172 EndY=57 EndZ=0
    g15: LineSegment StartX=-23.7172 StartY=57 StartZ=0 EndX=12 EndY=44 EndZ=0
    g16: LineSegment StartX=80.7172 StartY=57 StartZ=0 EndX=45 EndY=44 EndZ=0
    g17: LineSegment [constr] StartX=45 StartY=44 StartZ=0 EndX=12 EndY=44 EndZ=0
    g18: LineSegment StartX=12 StartY=44 StartZ=0 EndX=12 EndY=24 EndZ=0
    g19: LineSegment [constr] StartX=12 StartY=57 StartZ=0 EndX=12 EndY=44 EndZ=0
    g20: LineSegment [constr] StartX=45 StartY=44 StartZ=0 EndX=45 EndY=57 EndZ=0
    g21: GeomPoint [constr] X=0 Y=48.3676 Z=0
  constraints (63):
    c: Horizontal(g1)
    c: Symmetric(g1,g1,g2)
    c: PointOnObject(g2,g0)
    c: Vertical(g2)
    c: DistanceY(g2,g2) = 54
    c: Coincident(g0,g1)
    c: Coincident(g0,g1)
    c: Radius(g0) = 27.5
    c: PointOnObject(g3,g2)
    c: DistanceY(g2,g3) = 14
    c: PointOnObject(g4,g2)
    c: DistanceY(g2,g4) = 23
    c: Horizontal(g5)
    c: Coincident(g12,g7)
    c: Coincident(g18,g6)
    c: Horizontal(g6)
    c: Horizontal(g8)
    c: Vertical(g7)
    c: PointOnObject(g4,g6)
    c: Coincident(g5,g9)
    c: Vertical(g9)
    c: Coincident(g5,g10)
    c: PointOnObject(g10,g6)
    c: Vertical(g10)
    c: PointOnObject(g11,g-3)
    c: PointOnObject(g11,g0)
    c: Horizontal(g11)
    c: PointOnObject(g0,g11)
    c: Distance(g11,g7) = 11
    c: Coincident(g6,g9)
    c: Equal(g12,g6)
    c: Symmetric(g5,g5,g3)
    c: Horizontal(g12)
    c: Coincident(g12,g10)
    c: DistanceX(g5,g5) = 12
    c: Coincident(g8,g13)
    c: Horizontal(g13)
    c: Coincident(g8,g14)
    c: Horizontal(g14)
    c: Angle(g15,g13) = 0.349066
    c: DistanceY(g6,g15) = 20
    c: Coincident(g15,g13)
    c: Equal(g13,g14)
    c: Coincident(g14,g16)
    c: Coincident(g16,g17)
    c: Coincident(g17,g15)
    c: Horizontal(g17)
    c: Coincident(g7,g16)
    c: Coincident(g18,g15)
    c: Vertical(g18)
    c: Coincident(g8,g19)
    c: Coincident(g19,g15)
    c: Coincident(g7,g20)
    c: Coincident(g20,g8)
    c: Vertical(g20)
    c: Vertical(g19)
    c: Coincident(g0,g-4)
    c: PointOnObject(g8,g-5)
    c: PointOnObject(g21,g15)
    c: PointOnObject(g21,g-2)
    c: DistanceY(g9,g9) = 9
    c: DistanceX(g21,g15) = 12
    c: DistanceX(g17,g17) = 33
FEATURE [PartDesign::Pocket] Pocket016
  BaseFeature = -> Pad007
  Direction = (0,0,-1)
  Length = 5
  Length2 = 5
  Profile = -> Sketch026
  ReferenceAxis = -> Sketch026 [N_Axis]
  Refine = true
  Suppressed = false
  Type = 2
FEATURE [Sketcher::SketchObject] Sketch028
  ArcFitTolerance = 0
  AttachmentSupport = -> [Pocket016]
  ExternalGeometry = -> [Pocket016]
  FullyConstrained = true
  MakeInternals = false
  MapMode = 5
  Placement = pos=(0,0,5) rot=(0,0,1;0rad)
  sketch-geometry (7):
    g0: LineSegment [constr] StartX=37.5 StartY=7.5 StartZ=0 EndX=19.5 EndY=7.5 EndZ=0
    g1: GeomPoint X=28.5 Y=15 Z=0
    g2: GeomPoint X=28.5 Y=7.5 Z=0
    g3: LineSegment [constr] StartX=28.5 StartY=15 StartZ=0 EndX=28.5 EndY=7.5 EndZ=0
    g4: LineSegment [constr] StartX=28.5 StartY=0 StartZ=0 EndX=28.5 EndY=7.5 EndZ=0
    g5: Circle CenterX=19.5 CenterY=7.5 CenterZ=0 NormalX=0 NormalY=0 NormalZ=1 AngleXU=0 Radius=3.15
    g6: Circle CenterX=37.5 CenterY=7.5 CenterZ=0 NormalX=0 NormalY=0 NormalZ=1 AngleXU=0 Radius=3.15
  constraints (18):
    c: Horizontal(g0)
    c: Symmetric(g-3,g-3,g1)
    c: Symmetric(g0,g0,g2)
    c: Coincident(g3,g1)
    c: Coincident(g3,g2)
    c: Vertical(g3)
    c: PointOnObject(g4,g-1)
    c: Coincident(g4,g2)
    c: Vertical(g4)
    c: Equal(g4,g3)
    c: Coincident(g5,g0)
    c: Coincident(g6,g0)
    c: Diameter(g6) = 6.3
    c: Equal(g5,g6)
    c: DistanceX(g0,g0) = 18
    c: DistanceY(g0,g-3) = 7.5
    c: DistanceY(g0,g-4) = 40.8676
    c: DistanceY(g4,g0) = 7.5
FEATURE [PartDesign::Pocket] Pocket
  BaseFeature = -> Pocket016
  Direction = (0,0,-1)
  Length = 2
  Length2 = 5
  Profile = -> Sketch028
  ReferenceAxis = -> Sketch028 [N_Axis]
  Refine = true
  Suppressed = false
  Type = 0
FEATURE [Sketcher::SketchObject] Sketch041
  ArcFitTolerance = 1e-06
  AttachmentSupport = -> [Pocket]
  ExternalGeometry = -> [Pocket]
  FullyConstrained = true
  MakeInternals = false
  MapMode = 5
  Placement = pos=(0,0,3) rot=(0,0,1;0rad)
  sketch-geometry (2):
    g0: Circle CenterX=19.5 CenterY=7.5 CenterZ=0 NormalX=0 NormalY=0 NormalZ=1 AngleXU=0 Radius=1.3
    g1: Circle CenterX=37.5 CenterY=7.5 CenterZ=0 NormalX=0 NormalY=0 NormalZ=1 AngleXU=0 Radius=1.3
  constraints (4):
    c: Coincident(g0,g-4)
    c: Coincident(g1,g-3)
    c: Equal(g1,g0)
    c: Diameter(g0) = 2.6
FEATURE [PartDesign::Pocket] Pocket024
  BaseFeature = -> Pocket
  Direction = (0,0,-1)
  Length = 5
  Length2 = 5
  Profile = -> Sketch041
  ReferenceAxis = -> Sketch041 [N_Axis]
  Refine = true
  Suppressed = false
  Type = 2
FEATURE [PartDesign::Body] Body008  label="claw"
  AllowCompound = false
  Group = -> [Sketch025,Pad007,Sketch026,Pocket016,Sketch028,Pocket,Sketch041,Pocket024]
  Origin = -> Origin006
  Tip = -> Pocket024
COMPONENT P6 — recipe-attached ("claw-holder001", modeled in this document).
Construction recipe (the document's own serialized feature program — sketch geometry with constraints, then the solid features built on it; lengths are millimeters unless a unit is written):

FEATURE [Sketcher::SketchObject] Sketch037
  ArcFitTolerance = 0
  AttachmentSupport = -> [XY_Plane008]
  FullyConstrained = true
  MakeInternals = false
  MapMode = 5
  sketch-geometry (4):
    g0: LineSegment StartX=0 StartY=0 StartZ=0 EndX=0 EndY=15 EndZ=0
    g1: LineSegment StartX=0 StartY=15 StartZ=0 EndX=30 EndY=15 EndZ=0
    g2: LineSegment StartX=30 StartY=15 StartZ=0 EndX=30 EndY=-5.44826e-11 EndZ=0
    g3: LineSegment StartX=0 StartY=0 StartZ=0 EndX=30 EndY=-5.44826e-11 EndZ=0
  constraints (11):
    c: Vertical(g0)
    c: Coincident(g0,g1)
    c: Horizontal(g1)
    c: Coincident(g1,g2)
    c: Vertical(g2)
    c: Equal(g2,g0)
    c: Coincident(g0,g-1)
    c: DistanceX(g1,g1) = 30
    c: Coincident(g0,g3)
    c: Coincident(g3,g2)
    c: DistanceY(g2,g2) = 15
FEATURE [PartDesign::Pad] Pad012
  Direction = (0,0,1)
  Length = 5
  Length2 = 10
  Profile = -> Sketch037
  ReferenceAxis = -> Sketch037 [N_Axis]
  Refine = true
  Suppressed = false
  Type = 0
FEATURE [Sketcher::SketchObject] Sketch039
  ArcFitTolerance = 0
  ExternalGeometry = -> [Pad012]
  FullyConstrained = true
  MakeInternals = false
  MapMode = 5
  Placement = pos=(0,0,5) rot=(0,0,1;0rad)
  sketch-geometry (7):
    g0: LineSegment [constr] StartX=24 StartY=7.5 StartZ=0 EndX=6 EndY=7.5 EndZ=0
    g1: GeomPoint X=15 Y=15 Z=0
    g2: GeomPoint X=15 Y=7.5 Z=0
    g3: LineSegment [constr] StartX=15 StartY=15 StartZ=0 EndX=15 EndY=7.5 EndZ=0
    g4: LineSegment [constr] StartX=15 StartY=0 StartZ=0 EndX=15 EndY=7.5 EndZ=0
    g5: Circle CenterX=6 CenterY=7.5 CenterZ=0 NormalX=0 NormalY=0 NormalZ=1 AngleXU=0 Radius=3.15
    g6: Circle CenterX=24 CenterY=7.5 CenterZ=0 NormalX=0 NormalY=0 NormalZ=1 AngleXU=0 Radius=3.15
  constraints (16):
    c: Horizontal(g0)
    c: Symmetric(g0,g0,g2)
    c: Coincident(g3,g1)
    c: Coincident(g3,g2)
    c: Vertical(g3)
    c: PointOnObject(g4,g-1)
    c: Coincident(g4,g2)
    c: Vertical(g4)
    c: Equal(g4,g3)
    c: Coincident(g5,g0)
    c: Coincident(g6,g0)
    c: Diameter(g6) = 6.3
    c: Equal(g5,g6)
    c: DistanceX(g0,g0) = 18
    c: DistanceY(g4,g0) = 7.5
    c: Symmetric(g-3,g-3,g1)
FEATURE [PartDesign::Pocket] Pocket022
  BaseFeature = -> Pad012
  Direction = (0,0,-1)
  Length = 2
  Length2 = 5
  Profile = -> Sketch039
  ReferenceAxis = -> Sketch039 [N_Axis]
  Refine = true
  Suppressed = false
  Type = 0
FEATURE [Sketcher::SketchObject] Sketch040
  ArcFitTolerance = 1e-06
  AttachmentSupport = -> [Pocket022]
  ExternalGeometry = -> [Pocket022]
  FullyConstrained = true
  MakeInternals = false
  MapMode = 5
  Placement = pos=(0,0,3) rot=(0,0,1;0rad)
  sketch-geometry (2):
    g0: Circle CenterX=24 CenterY=7.5 CenterZ=0 NormalX=0 NormalY=0 NormalZ=1 AngleXU=0 Radius=1.3
    g1: Circle CenterX=6 CenterY=7.5 CenterZ=0 NormalX=0 NormalY=0 NormalZ=1 AngleXU=0 Radius=1.3
  constraints (4):
    c: Coincident(g0,g-3)
    c: Coincident(g1,g-4)
    c: Equal(g0,g1)
    c: Diameter(g0) = 2.6
FEATURE [PartDesign::Pocket] Pocket023
  BaseFeature = -> Pocket022
  Direction = (0,0,-1)
  Length = 5
  Length2 = 5
  Profile = -> Sketch040
  ReferenceAxis = -> Sketch040 [N_Axis]
  Refine = true
  Suppressed = false
  Type = 2
FEATURE [PartDesign::Fillet] Fillet001
  Base = -> Pocket023 [Edge5,Edge1,Edge2,Edge8]
  BaseFeature = -> Pocket023
  Radius = 3
  Refine = true
  SupportTransform = false
  Suppressed = false
  UseAllEdges = false
FEATURE [PartDesign::Body] Body010  label="claw-holder"
  AllowCompound = false
  Group = -> [Sketch037,Pad012,Sketch039,Pocket022,Sketch040,Pocket023,Fillet001]
  Origin = -> Origin008
  Tip = -> Fillet001
COMPONENT P7 — recipe-attached ("rod001", modeled in this document).
Construction recipe (the document's own serialized feature program — sketch geometry with constraints, then the solid features built on it; lengths are millimeters unless a unit is written):

FEATURE [Sketcher::SketchObject] Sketch030
  ArcFitTolerance = 0
  AttachmentSupport = -> [XY_Plane007]
  FullyConstrained = true
  MakeInternals = false
  MapMode = 5
  sketch-geometry (1):
    g0: Circle CenterX=0 CenterY=0 CenterZ=0 NormalX=0 NormalY=0 NormalZ=1 AngleXU=0 Radius=3
  constraints (2):
    c: Coincident(g0,g-1)
    c: Diameter(g0) = 6
FEATURE [PartDesign::Pad] Pad009
  Direction = (0,0,1)
  Length = 30
  Length2 = 10
  Profile = -> Sketch030
  ReferenceAxis = -> Sketch030 [N_Axis]
  Refine = true
  Suppressed = false
  Type = 0
FEATURE [PartDesign::Body] Body009  label="rod"
  AllowCompound = false
  Group = -> [Sketch030,Pad009]
  Origin = -> Origin007
  Tip = -> Pad009
COMPONENT P8 — same part as P7; its construction recipe is shown at P7.
PROVENANCE & LICENSES
A FreeCAD (.FCStd) document from a public repository crawl; recipes are the document's own serialized feature recipes (and, for linked parts, companion documents' recipes).
License: gpl-3.0.
